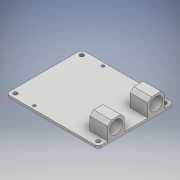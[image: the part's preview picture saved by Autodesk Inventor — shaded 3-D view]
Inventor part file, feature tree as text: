
AUTODESK INVENTOR PART (.ipt)
format: ipt  version: 2018.3 (Build 223284000, 284)  size: 176,640 bytes
history: native  units: mm
features: extrude x3, sketch x3, chamfer x1
ambient origin geometry x8: Origin, YZ Plane, XZ Plane, XY Plane, X Axis, Y Axis, Z Axis, Center Point
bodies: Solid1 (feature_tree)
feature tree (7):
  extrude  "Extrusion1"  Depth=64.0mm
  extrude  "Extrusion2"  Depth=2.0mm
  extrude  "Extrusion3"  Depth=2.0mm
  chamfer  "Chamfer1"  Distance=2.0mm
  sketch  "Sketch1"  dims[d0=78.0mm d1=64.0mm]
  sketch  "Sketch2"  dims[d2=2.0mm d3=2.0mm]
  sketch  "Sketch3"  dims[d4=2.0mm d5=2.0mm d6=2.0mm d7=2.0mm d8=2.0mm d9=2.0mm d10=2.5mm d11=21.0mm d12=3.0mm d13=2.5mm d14=3.0mm d15=21.0mm d16=3.5mm d17=4.0mm d18=4.0mm d19=3.5mm d20=4.0mm d21=4.0mm d22=3.5mm d23=4.0mm d24=4.0mm d25=3.5mm d26=4.0mm d27=4.0mm d28=2.0mm d29=0.0mm d30=15.0mm d31=14.0mm d32=8.0mm d33=14.0mm d34=8.0mm d35=14.0mm d36=0.0mm d37=11.0mm d38=7.0mm d39=7.0mm d40=11.0mm d41=7.0mm d42=7.0mm d43=14.0mm d44=0.0mm d45=3.0mm d46=2.0mm d47=45.0deg]
